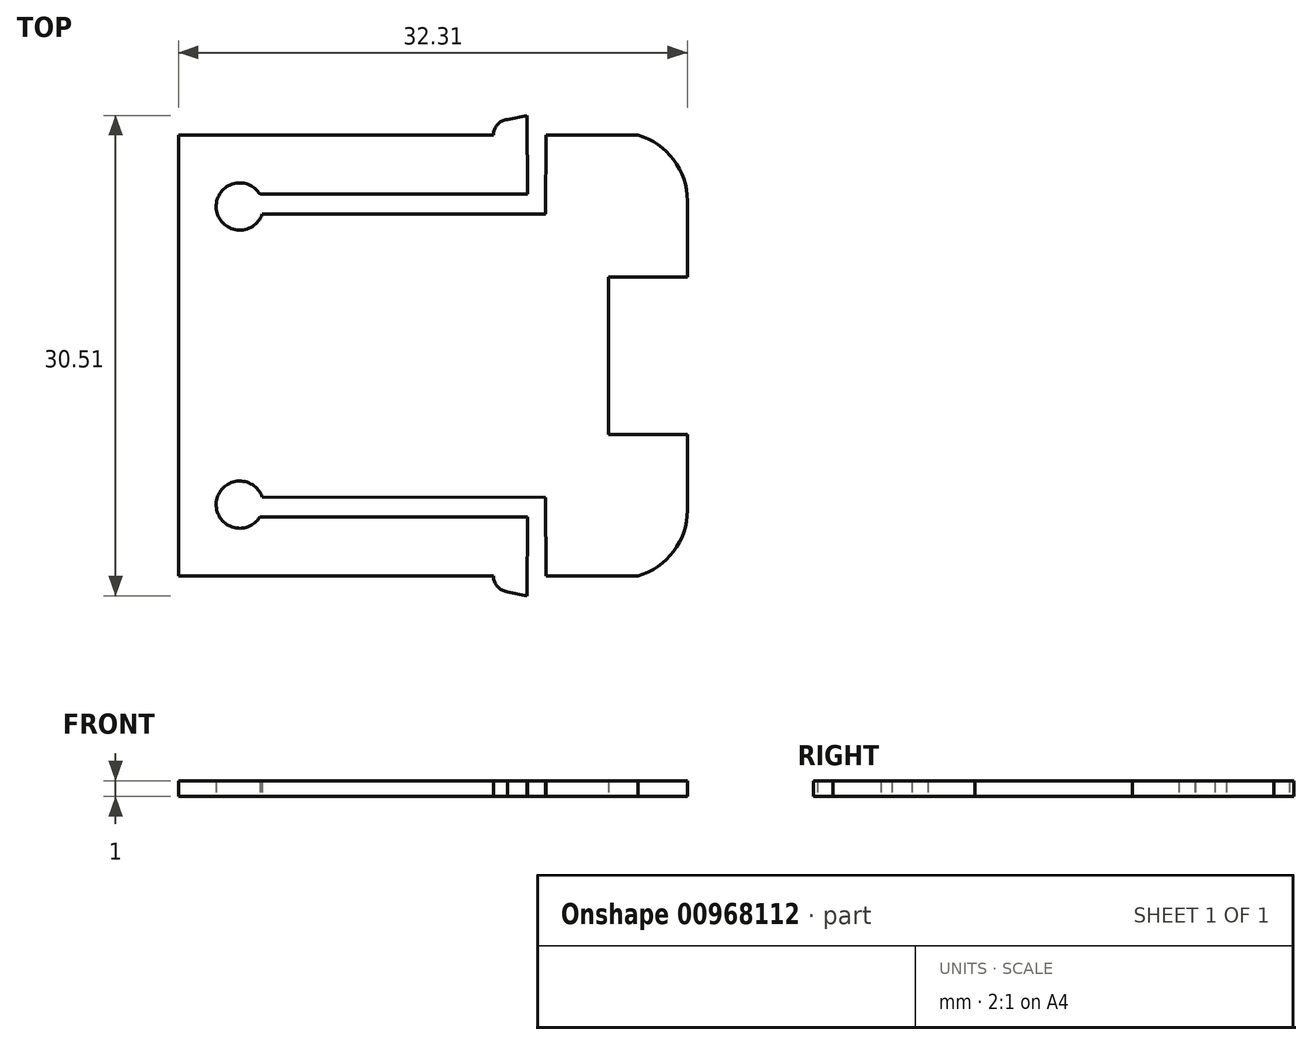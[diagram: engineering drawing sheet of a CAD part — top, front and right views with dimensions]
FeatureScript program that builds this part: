
annotation { "Feature Type Name" : "Feature", "Feature Type Description" : "" }
export const myFeature = defineFeature(function(context is Context, id is Id, definition is map)
    precondition{}
    {
        {
            var Q0;
            Q0=qCreatedBy(makeId("Top.planeOp"),FACE);
            var sketch = newSketch(context, id + "F0", { "sketchPlane" : qUnion([Q0])});
            skLineSegment(sketch, "E0", {"start": v(7.45, 13.66) * mm, "end": v(13.3, 13.66) * mm});
            skLineSegment(sketch, "E1", {"start": v(11.42, 4.66) * mm, "end": v(16.42, 4.66) * mm});
            skLineSegment(sketch, "E2", {"start": v(5, 14.66) * mm, "end": v(6.23, 14.91) * mm});
            skArc(sketch, "E3", {"start": v(-10.72, 9.9) * mm, "mid": v(-13.5, 8.96) * mm, "end": v(-10.58, 8.64) * mm});
            skLineSegment(sketch, "E4", {"start": v(16.42, 4.66) * mm, "end": v(16.42, 9.48) * mm});
            skArc(sketch, "E5", {"start": v(16.42, 9.48) * mm, "mid": v(15.55, 12.1) * mm, "end": v(13.3, 13.66) * mm});
            skLineSegment(sketch, "E6.MirrorCS", {"start": v(11.42, -5.34) * mm, "end": v(16.42, -5.34) * mm});
            skLineSegment(sketch, "E7", {"start": v(11.42, 4.66) * mm, "end": v(11.42, -5.34) * mm});
            skLineSegment(sketch, "E8", {"start": v(-15.89, 13.66) * mm, "end": v(-15.89, -14.34) * mm});
            skLineSegment(sketch, "E9", {"start": v(-10.58, 8.64) * mm, "end": v(7.42, 8.66) * mm});
            skArc(sketch, "E10", {"start": v(5, 14.66) * mm, "mid": v(4.37, 14.33) * mm, "end": v(4.11, 13.66) * mm});
            skLineSegment(sketch, "E11", {"start": v(4.11, 13.66) * mm, "end": v(-15.89, 13.66) * mm});
            skLineSegment(sketch, "E12", {"start": v(6.23, 14.91) * mm, "end": v(6.28, 9.91) * mm});
            skLineSegment(sketch, "E13", {"start": v(-10.72, 9.9) * mm, "end": v(6.28, 9.91) * mm});
            skLineSegment(sketch, "E14", {"start": v(7.42, 8.66) * mm, "end": v(7.45, 13.66) * mm});
            skLineSegment(sketch, "E15", {"start": v(12.94, 4.66) * mm, "end": v(12.94, 13.66) * mm});
            skLineSegment(sketch, "E16.MirrorCS", {"start": v(16.42, -5.34) * mm, "end": v(16.42, -10.17) * mm});
            skArc(sketch, "E17.MirrorCS", {"start": v(16.42, -10.17) * mm, "mid": v(15.55, -12.78) * mm, "end": v(13.3, -14.34) * mm});
            skLineSegment(sketch, "E18.MirrorCS", {"start": v(7.45, -14.34) * mm, "end": v(13.3, -14.34) * mm});
            skLineSegment(sketch, "E19.MirrorCS", {"start": v(7.42, -9.34) * mm, "end": v(7.45, -14.34) * mm});
            skLineSegment(sketch, "E20.MirrorCS", {"start": v(-10.58, -9.33) * mm, "end": v(7.42, -9.34) * mm});
            skLineSegment(sketch, "E21.MirrorCS", {"start": v(-10.72, -10.6) * mm, "end": v(6.28, -10.6) * mm});
            skLineSegment(sketch, "E22.MirrorCS", {"start": v(6.23, -15.6) * mm, "end": v(6.28, -10.6) * mm});
            skLineSegment(sketch, "E23.MirrorCS", {"start": v(5, -15.34) * mm, "end": v(6.23, -15.6) * mm});
            skArc(sketch, "E24.MirrorCS", {"start": v(5, -15.34) * mm, "mid": v(4.37, -15.01) * mm, "end": v(4.11, -14.34) * mm});
            skLineSegment(sketch, "E25.MirrorCS", {"start": v(4.11, -14.34) * mm, "end": v(-15.89, -14.34) * mm});
            skArc(sketch, "E26.MirrorCS", {"start": v(-10.72, -10.6) * mm, "mid": v(-13.5, -9.65) * mm, "end": v(-10.58, -9.33) * mm});
            skSolve(sketch);
        }
        {
            var Q0;
            Q0 = qSketchRegion(id + "F0", true);
            extrude(context, id + "F1", {"entities" : qUnion([Q0]), "depth" : 1 * mm, "offsetDistance" : 25.4 * mm});
        }
    });
